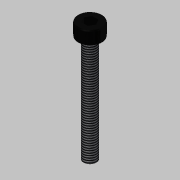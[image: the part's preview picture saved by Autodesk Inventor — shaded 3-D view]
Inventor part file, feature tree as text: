
AUTODESK INVENTOR PART (.ipt)
format: ipt  version: 2014 (Build 180170000, 170)  size: 111,104 bytes
history: native  units: mm
features: extrude x4, sketch x4, fillet x1, thread x1, reference x1
ambient origin geometry x8: Origin, YZ Plane, XZ Plane, XY Plane, X Axis, Y Axis, Z Axis, Center Point
bodies: Solid1 (feature_tree)
feature tree (11):
  extrude  "Extrusion1"  Depth=25.0mm TaperAngle=0.0deg
  extrude  "Extrusion2"  Depth=3.0mm TaperAngle=0.0deg
  fillet  "Fillet1"  Radius=0.3mm
  extrude  "Extrusion3"  Depth=0.5mm TaperAngle=0.0deg
  extrude  "Extrusion4"  Depth=2.0mm TaperAngle=0.0deg
  thread  "Thread1"  [1 undecoded]
  sketch  "Sketch1"  dims[d0=3.0mm d1=25.0mm d2=0.0mm]
  reference  "Reference1"
  sketch  "Sketch2"  dims[d3=5.6mm d4=3.0mm d5=0.0mm d6=0.3mm]
  sketch  "Sketch3"  dims[d7=5.5mm d8=0.5mm d9=0.0mm]
  sketch  "Sketch4"  dims[d10=2.5mm d11=2.0mm d12=0.0mm d13=10.0mm d14=0.0mm]
note: 1 required parameter value undecoded (feature->parameter linkage not recoverable at this tier; creation-order binding heuristic only, values carry confidence <= 0.55)
